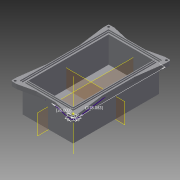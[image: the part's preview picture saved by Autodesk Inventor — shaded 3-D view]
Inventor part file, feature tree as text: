
AUTODESK INVENTOR PART (.ipt)
format: ipt  version: 2015 SP2 (Build 190223200, 223)  size: 288,768 bytes
history: native  units: in
note: dims shown in document units (in); Inventor stores cm internally (conversion verified against a paired STEP export)
features: sketch x8, extrude x7, projected_geometry x7, plane x3, hole x2, fillet x2, mirror x2, other x1
ambient origin geometry x8: Origin, YZ Plane, XZ Plane, XY Plane, X Axis, Y Axis, Z Axis, Center Point
bodies: Solid1 (feature_tree)
feature tree (32):
  extrude  "Extrusion1"  Depth=4.6489in
  extrude  "Extrusion2"  Depth=0.0394in
  extrude  "Extrusion3"  Depth=0.0394in
  extrude  "Extrusion4"  Depth=0.0394in
  extrude  "Extrusion6"  Depth=0.0394in TaperAngle=0.0deg
  extrude  "Extrusion5"  Depth=0.0394in
  hole  "Hole1"  [1 undecoded]
  fillet  "Fillet1"  Radius=0.315in
  extrude  "Extrusion7"  Depth=0.2362in
  fillet  "Fillet2"  Radius=4.6489in
  sketch  "Sketch12"  dims[d19=0.0787in d20=0.0in d21=0.2362in d22=0.1181in d23=0.2362in d24=0.1575in d25=0.0787in d26=90.0deg d27=0.315in d28=0.8108in d29=4.6489in d30=0.0787in d31=0.1181in d32=0.0394in d33=0.1181in d34=0.2362in d35=0.1181in d36=0.1181in d37=45.0deg d47=1.0237in d50=0.0394in d51=0.0394in d52=0.1181in d53=0.0394in d54=0.0in d55=0.0in d56=0.2362in d57=0.2362in d58=0.1575in d59=0.0in d60=0.0787in d61=0.1181in d62=0.1181in d63=0.2362in d64=0.1575in d65=0.0787in d66=90.0deg d67=0.315in d68=0.8108in d69=2.415in d70=4.334in]
  other  "Work Point1"
  hole  "Hole2"  [1 undecoded]
  plane  "Work Plane1"
  plane  "Work Plane5"
  plane  "Work Plane6"
  mirror  "Mirror6"
  mirror  "Mirror7"
  sketch  "Sketch1"  dims[d0=2.7299in d1=4.6489in]
  sketch  "Sketch2"  dims[d2=0.0394in d3=0.0in d4=0.0394in]
  projected_geometry  "Projected Loop1"
  sketch  "Sketch3"  dims[d5=1.378in d6=0.0in d7=0.0394in]
  projected_geometry  "Projected Loop2"
  sketch  "Sketch4"  dims[d8=0.0394in d9=0.0394in]
  projected_geometry  "Projected Loop3"
  sketch  "Sketch5"  dims[d10=0.0394in d11=0.0394in d12=0.0in]
  projected_geometry  "Projected Loop4"
  sketch  "Sketch10"  dims[d13=0.0394in d14=0.0394in]
  projected_geometry  "Projected Loop5"
  projected_geometry  "Projected Loop6"
  projected_geometry  "Projected Loop7"
  sketch  "Sketch11"  dims[d15=0.0591in d16=0.0in d17=0.315in d18=0.315in]
note: 2 required parameter values undecoded (feature->parameter linkage not recoverable at this tier; creation-order binding heuristic only, values carry confidence <= 0.55)
